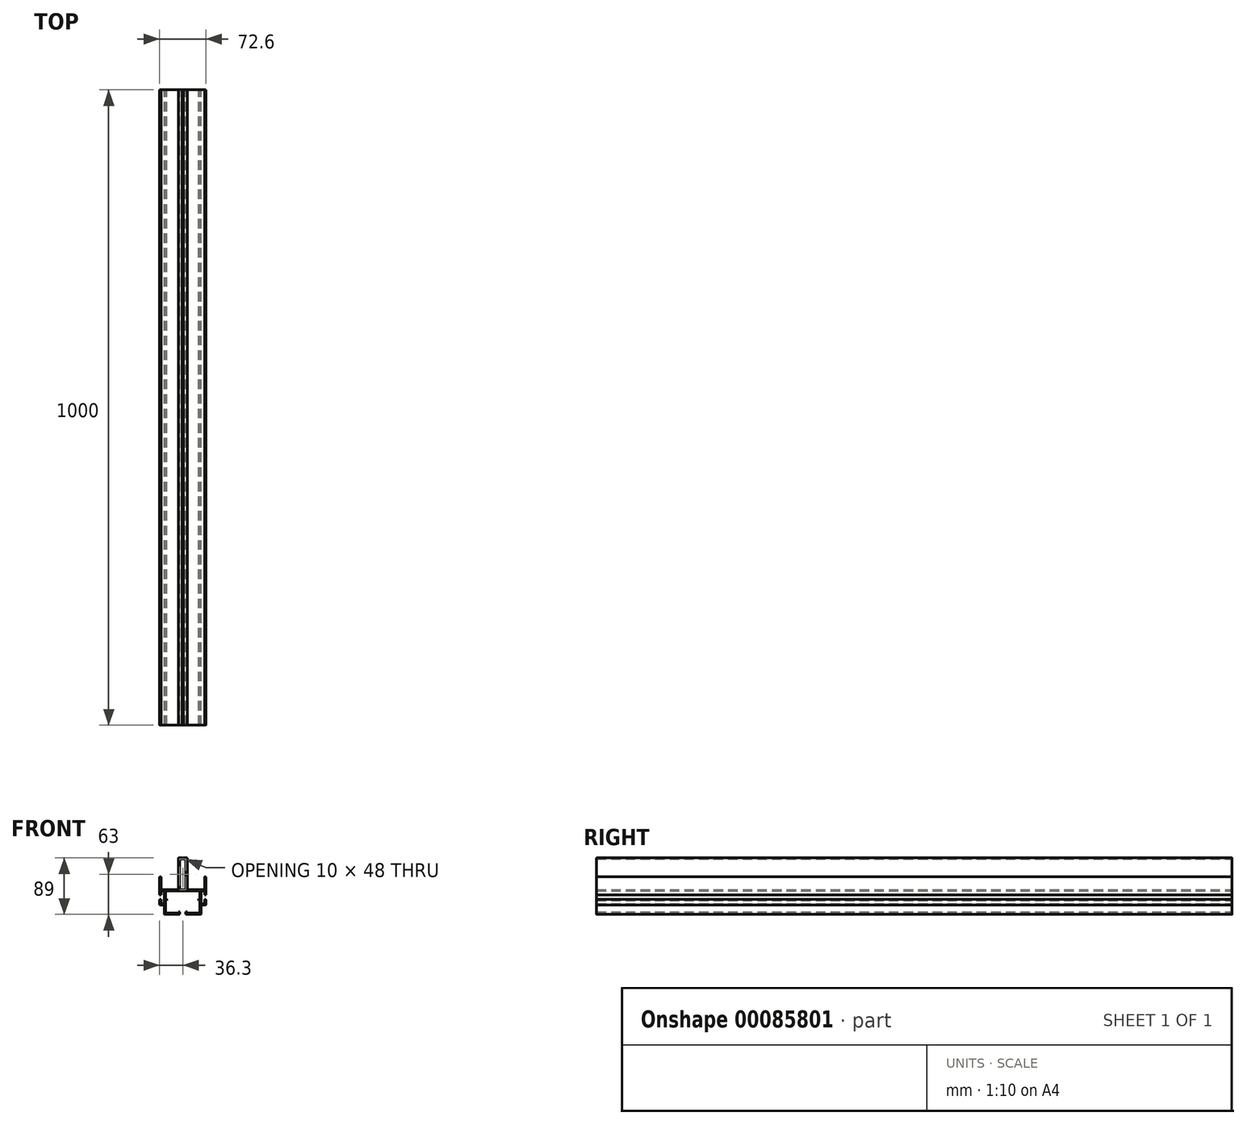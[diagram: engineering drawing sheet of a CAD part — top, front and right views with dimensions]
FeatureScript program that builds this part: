
annotation { "Feature Type Name" : "Feature", "Feature Type Description" : "" }
export const myFeature = defineFeature(function(context is Context, id is Id, definition is map)
    precondition{}
    {
        {
            var Q0;
            Q0=qCreatedBy(makeId("Front.planeOp"),FACE);
            var sketch = newSketch(context, id + "F0", { "sketchPlane" : qUnion([Q0])});
            skLineSegment(sketch, "E0", {"start": v(0, -3) * mm, "end": v(-7, -3) * mm});
            skLineSegment(sketch, "E1", {"start": v(-7, -3) * mm, "end": v(-7, -53) * mm});
            skLineSegment(sketch, "E2", {"start": v(-7, -53) * mm, "end": v(-34.3, -53) * mm});
            skLineSegment(sketch, "E3", {"start": v(-34.3, -53) * mm, "end": v(-34.3, -33) * mm});
            skLineSegment(sketch, "E4", {"start": v(-34.3, -33) * mm, "end": v(-36.3, -33) * mm});
            skLineSegment(sketch, "E5", {"start": v(-34.3, -55) * mm, "end": v(-29.1, -55) * mm});
            skLineSegment(sketch, "E6", {"start": v(-29.1, -55) * mm, "end": v(-29.1, -75) * mm});
            skLineSegment(sketch, "E7", {"start": v(-29.1, -75) * mm, "end": v(-34.3, -75) * mm});
            skLineSegment(sketch, "E8", {"start": v(-29.1, -92) * mm, "end": v(-5, -92) * mm});
            skLineSegment(sketch, "E9", {"start": v(-5, -92) * mm, "end": v(-5, -88) * mm});
            skLineSegment(sketch, "E10", {"start": v(-5, -88) * mm, "end": v(-7, -88) * mm});
            skLineSegment(sketch, "E11", {"start": v(-7, -88) * mm, "end": v(-7, -90) * mm});
            skLineSegment(sketch, "E12", {"start": v(-7, -90) * mm, "end": v(-27.1, -90) * mm});
            skLineSegment(sketch, "E13", {"start": v(-27.1, -90) * mm, "end": v(-27.1, -69.9) * mm});
            skLineSegment(sketch, "E14", {"start": v(-27.1, -69.9) * mm, "end": v(-25.1, -69.9) * mm});
            skLineSegment(sketch, "E15", {"start": v(-25.1, -69.9) * mm, "end": v(-25.1, -67.9) * mm});
            skLineSegment(sketch, "E16", {"start": v(-25.1, -67.9) * mm, "end": v(-27.1, -67.9) * mm});
            skLineSegment(sketch, "E17", {"start": v(-27.1, -67.9) * mm, "end": v(-27.1, -55) * mm});
            skLineSegment(sketch, "E18", {"start": v(-27.1, -55) * mm, "end": v(0, -55) * mm});
            skLineSegment(sketch, "E19", {"start": v(0, -5) * mm, "end": v(0, -3) * mm});
            skLineSegment(sketch, "E20", {"start": v(0, -5) * mm, "end": v(-5, -5) * mm});
            skLineSegment(sketch, "E21", {"start": v(-5, -5) * mm, "end": v(-5, -53) * mm});
            skLineSegment(sketch, "E22", {"start": v(-5, -53) * mm, "end": v(0, -53) * mm});
            skLineSegment(sketch, "E23", {"start": v(0, -53) * mm, "end": v(0, -55) * mm});
            skLineSegment(sketch, "E24", {"start": v(-36.3, -33) * mm, "end": v(-36.3, -61.5) * mm});
            skLineSegment(sketch, "E25", {"start": v(-36.3, -61.5) * mm, "end": v(-34.3, -61.5) * mm});
            skLineSegment(sketch, "E26", {"start": v(-34.3, -61.5) * mm, "end": v(-34.3, -55) * mm});
            skLineSegment(sketch, "E27", {"start": v(-34.3, -75) * mm, "end": v(-34.3, -68.5) * mm});
            skLineSegment(sketch, "E28", {"start": v(-34.3, -68.5) * mm, "end": v(-36.3, -68.5) * mm});
            skLineSegment(sketch, "E29", {"start": v(-36.3, -68.5) * mm, "end": v(-36.3, -77) * mm});
            skLineSegment(sketch, "E30", {"start": v(-36.3, -77) * mm, "end": v(-29.1, -77) * mm});
            skLineSegment(sketch, "E31", {"start": v(-29.1, -77) * mm, "end": v(-29.1, -92) * mm});
            skSolve(sketch);
        }
        {
            var Q0;
            Q0=makeQuery(id+"F0.imprint","IMPRINT",FACE,{"disambiguationData":[TD([[makeQuery(id+"F0.imprint","IMPRINT",EDGE,{"derivedFrom":sQuery(id+"F0.wireOp",EDGE,"E0")}),1.0]])]});
            extrude(context, id + "F1", {"entities" : qUnion([Q0]), "depth" : 1000 * mm});
        }
        {
            var Q0;
            Q0=makeQuery(id+"F1.opExtrude","SWEPT_EDGE",EDGE,{"disambiguationData":[OSD([sQuery(id+"F0.wireOp",EDGE,"E4"),sQuery(id+"F0.wireOp",EDGE,"E24")])]});
            var Q1;
            Q1=makeQuery(id+"F1.opExtrude","SWEPT_EDGE",EDGE,{"disambiguationData":[OSD([sQuery(id+"F0.wireOp",EDGE,"E28"),sQuery(id+"F0.wireOp",EDGE,"E29")])]});
            var Q2;
            Q2=makeQuery(id+"F1.opExtrude","SWEPT_EDGE",EDGE,{"disambiguationData":[OSD([sQuery(id+"F0.wireOp",EDGE,"E8"),sQuery(id+"F0.wireOp",EDGE,"E9")])]});
            var Q3;
            Q3=makeQuery(id+"F1.opExtrude","SWEPT_EDGE",EDGE,{"disambiguationData":[OSD([sQuery(id+"F0.wireOp",EDGE,"E9"),sQuery(id+"F0.wireOp",EDGE,"E10")])]});
            var Q4;
            Q4=makeQuery(id+"F1.opExtrude","SWEPT_EDGE",EDGE,{"disambiguationData":[OSD([sQuery(id+"F0.wireOp",EDGE,"E0"),sQuery(id+"F0.wireOp",EDGE,"E1")])]});
            var Q5;
            Q5=makeQuery(id+"F1.opExtrude","SWEPT_EDGE",EDGE,{"disambiguationData":[OSD([sQuery(id+"F0.wireOp",EDGE,"E3"),sQuery(id+"F0.wireOp",EDGE,"E4")])]});
            var Q6;
            Q6=makeQuery(id+"F1.opExtrude","SWEPT_EDGE",EDGE,{"disambiguationData":[OSD([sQuery(id+"F0.wireOp",EDGE,"E21"),sQuery(id+"F0.wireOp",EDGE,"E22")])]});
            var Q7;
            Q7=makeQuery(id+"F1.opExtrude","SWEPT_EDGE",EDGE,{"disambiguationData":[OSD([sQuery(id+"F0.wireOp",EDGE,"E15"),sQuery(id+"F0.wireOp",EDGE,"E16")])]});
            var Q8;
            Q8=makeQuery(id+"F1.opExtrude","SWEPT_EDGE",EDGE,{"disambiguationData":[OSD([sQuery(id+"F0.wireOp",EDGE,"E8"),sQuery(id+"F0.wireOp",EDGE,"E31")])]});
            var Q9;
            Q9=makeQuery(id+"F1.opExtrude","SWEPT_EDGE",EDGE,{"disambiguationData":[OSD([sQuery(id+"F0.wireOp",EDGE,"E29"),sQuery(id+"F0.wireOp",EDGE,"E30")])]});
            var Q10;
            Q10=makeQuery(id+"F1.opExtrude","SWEPT_EDGE",EDGE,{"disambiguationData":[OSD([sQuery(id+"F0.wireOp",EDGE,"E24"),sQuery(id+"F0.wireOp",EDGE,"E25")])]});
            var Q11;
            Q11=makeQuery(id+"F1.opExtrude","SWEPT_EDGE",EDGE,{"disambiguationData":[OSD([sQuery(id+"F0.wireOp",EDGE,"E1"),sQuery(id+"F0.wireOp",EDGE,"E2")])]});
            fillet(context, id + "F2", {"entities" : qUnion([Q0, Q1, Q2, Q3, Q4, Q5, Q6, Q7, Q8, Q9, Q10, Q11]), "radius" : 0.5 * mm, "tangentPropagation" : true, "allowEdgeOverflow" : false});
        }
        {
            var Q0;
            Q0=makeQuery(id+"F1.opExtrude","SWEPT_BODY",BODY,{"disambiguationData":[OSD([sQuery(id+"F0.wireOp",EDGE,"E0"),sQuery(id+"F0.wireOp",EDGE,"E1"),sQuery(id+"F0.wireOp",EDGE,"E2"),sQuery(id+"F0.wireOp",EDGE,"E3"),sQuery(id+"F0.wireOp",EDGE,"E4"),sQuery(id+"F0.wireOp",EDGE,"E5"),sQuery(id+"F0.wireOp",EDGE,"E6"),sQuery(id+"F0.wireOp",EDGE,"E7"),sQuery(id+"F0.wireOp",EDGE,"E8"),sQuery(id+"F0.wireOp",EDGE,"E9"),sQuery(id+"F0.wireOp",EDGE,"E10"),sQuery(id+"F0.wireOp",EDGE,"E11"),sQuery(id+"F0.wireOp",EDGE,"E12"),sQuery(id+"F0.wireOp",EDGE,"E13"),sQuery(id+"F0.wireOp",EDGE,"E14"),sQuery(id+"F0.wireOp",EDGE,"E15"),sQuery(id+"F0.wireOp",EDGE,"E16"),sQuery(id+"F0.wireOp",EDGE,"E17"),sQuery(id+"F0.wireOp",EDGE,"E18"),sQuery(id+"F0.wireOp",EDGE,"E19"),sQuery(id+"F0.wireOp",EDGE,"E20"),sQuery(id+"F0.wireOp",EDGE,"E21"),sQuery(id+"F0.wireOp",EDGE,"E22"),sQuery(id+"F0.wireOp",EDGE,"E23"),sQuery(id+"F0.wireOp",EDGE,"E24"),sQuery(id+"F0.wireOp",EDGE,"E25"),sQuery(id+"F0.wireOp",EDGE,"E26"),sQuery(id+"F0.wireOp",EDGE,"E27"),sQuery(id+"F0.wireOp",EDGE,"E28"),sQuery(id+"F0.wireOp",EDGE,"E29"),sQuery(id+"F0.wireOp",EDGE,"E30"),sQuery(id+"F0.wireOp",EDGE,"E31")])]});
            var Q1;
            Q1=qCreatedBy(makeId("Right.planeOp"),FACE);
            mirror(context, id + "F3", {"operationType" : NewBodyOperationType.ADD, "entities" : qUnion([Q0]), "mirrorPlane" : qUnion([Q1])});
        }
        {
            var Q0;
            {var subQ0=makeQuery(id+"F1.opExtrude","CAP_FACE",FACE,{"disambiguationData":[OSD([sQuery(id+"F0.wireOp",EDGE,"E0"),sQuery(id+"F0.wireOp",EDGE,"E1"),sQuery(id+"F0.wireOp",EDGE,"E2"),sQuery(id+"F0.wireOp",EDGE,"E3"),sQuery(id+"F0.wireOp",EDGE,"E4"),sQuery(id+"F0.wireOp",EDGE,"E5"),sQuery(id+"F0.wireOp",EDGE,"E6"),sQuery(id+"F0.wireOp",EDGE,"E7"),sQuery(id+"F0.wireOp",EDGE,"E8"),sQuery(id+"F0.wireOp",EDGE,"E9"),sQuery(id+"F0.wireOp",EDGE,"E10"),sQuery(id+"F0.wireOp",EDGE,"E11"),sQuery(id+"F0.wireOp",EDGE,"E12"),sQuery(id+"F0.wireOp",EDGE,"E13"),sQuery(id+"F0.wireOp",EDGE,"E14"),sQuery(id+"F0.wireOp",EDGE,"E15"),sQuery(id+"F0.wireOp",EDGE,"E16"),sQuery(id+"F0.wireOp",EDGE,"E17"),sQuery(id+"F0.wireOp",EDGE,"E18"),sQuery(id+"F0.wireOp",EDGE,"E19"),sQuery(id+"F0.wireOp",EDGE,"E20"),sQuery(id+"F0.wireOp",EDGE,"E21"),sQuery(id+"F0.wireOp",EDGE,"E22"),sQuery(id+"F0.wireOp",EDGE,"E23"),sQuery(id+"F0.wireOp",EDGE,"E24"),sQuery(id+"F0.wireOp",EDGE,"E25"),sQuery(id+"F0.wireOp",EDGE,"E26"),sQuery(id+"F0.wireOp",EDGE,"E27"),sQuery(id+"F0.wireOp",EDGE,"E28"),sQuery(id+"F0.wireOp",EDGE,"E29"),sQuery(id+"F0.wireOp",EDGE,"E30"),sQuery(id+"F0.wireOp",EDGE,"E31")])],"isStart":false});Q0=makeQuery(id+"F3.boolean.opBoolean","MERGE",FACE,{"derivedFrom":[subQ0,makeQuery(id+"F3.opPattern","COPY",FACE,{"derivedFrom":subQ0,"instanceName":"1"})]});}
            var sketch = newSketch(context, id + "F4", { "sketchPlane" : qUnion([Q0])});
            skLineSegment(sketch, "E32", {"start": v(0, -3) * mm, "end": v(0, -3.5) * mm});
            skPoint(sketch, "E32.endSnap0", {"position": v(0, -3) * mm});
            skLineSegment(sketch, "E33", {"start": v(0, -3.5) * mm, "end": v(-0.83, -3) * mm});
            skLineSegment(sketch, "E34", {"start": v(-0.83, -3) * mm, "end": v(0, -3) * mm});
            skLineSegment(sketch, "E35", {"start": v(0, -3) * mm, "end": v(0.83, -3) * mm});
            skLineSegment(sketch, "E36", {"start": v(0.83, -3) * mm, "end": v(0, -3.5) * mm});
            skSolve(sketch);
        }
        {
            var Q0;
            Q0=makeQuery(id+"F4.imprint","IMPRINT",FACE,{"disambiguationData":[TD([[makeQuery(id+"F4.imprint","IMPRINT",EDGE,{"derivedFrom":sQuery(id+"F4.wireOp",EDGE,"E32")}),-1.0]])]});
            var Q1;
            Q1=makeQuery(id+"F4.imprint","IMPRINT",FACE,{"disambiguationData":[TD([[makeQuery(id+"F4.imprint","IMPRINT",EDGE,{"derivedFrom":sQuery(id+"F4.wireOp",EDGE,"E32")}),1.0]])]});
            extrude(context, id + "F5", {"entities" : qUnion([Q0, Q1]), "operationType" : NewBodyOperationType.REMOVE, "oppositeDirection" : true, "depth" : 1000 * mm});
        }
    });
